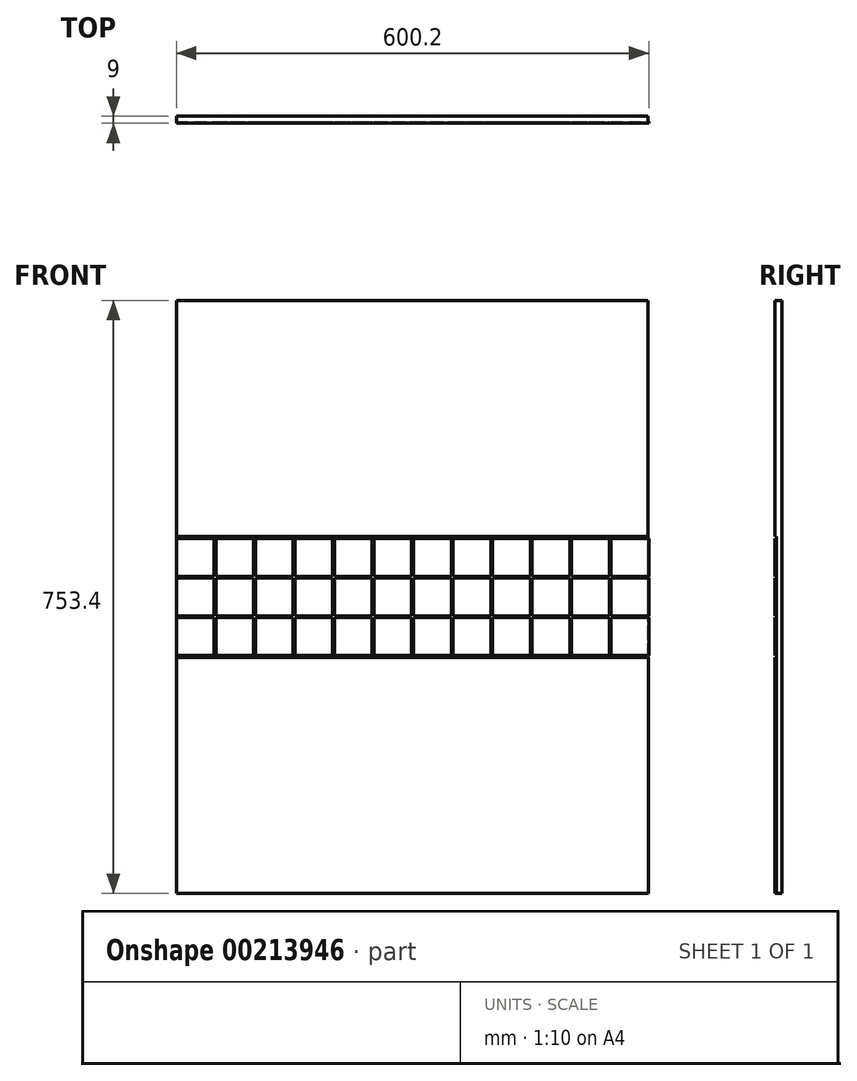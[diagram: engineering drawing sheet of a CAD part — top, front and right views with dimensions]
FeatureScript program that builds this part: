
annotation { "Feature Type Name" : "Feature", "Feature Type Description" : "" }
export const myFeature = defineFeature(function(context is Context, id is Id, definition is map)
    precondition{}
    {
        {
            var Q0;
            Q0=qCreatedBy(makeId("Front.planeOp"),FACE);
            var sketch = newSketch(context, id + "F0", { "sketchPlane" : qUnion([Q0])});
            skLineSegment(sketch, "E0.bottom", {"start": v(0, 0) * mm, "end": v(600, 0) * mm});
            skLineSegment(sketch, "E0.top", {"start": v(0, 300) * mm, "end": v(600, 300) * mm});
            skLineSegment(sketch, "E0.left", {"start": v(0, 0) * mm, "end": v(0, 300) * mm});
            skLineSegment(sketch, "E0.right", {"start": v(600, 0) * mm, "end": v(600, 300) * mm});
            skLineSegment(sketch, "E1.bottom", {"start": v(0, 350.5) * mm, "end": v(48, 350.5) * mm});
            skLineSegment(sketch, "E1.top", {"start": v(0, 302.5) * mm, "end": v(48, 302.5) * mm});
            skLineSegment(sketch, "E1.left", {"start": v(0, 302.5) * mm, "end": v(0, 350.5) * mm});
            skLineSegment(sketch, "E1.right", {"start": v(48, 302.5) * mm, "end": v(48, 350.5) * mm});
            skLineSegment(sketch, "E2.bottom", {"start": v(0, 453.4) * mm, "end": v(599.37, 453.4) * mm});
            skLineSegment(sketch, "E2.top", {"start": v(0, 753.4) * mm, "end": v(599.37, 753.4) * mm});
            skLineSegment(sketch, "E2.left", {"start": v(0, 453.4) * mm, "end": v(0, 753.4) * mm});
            skLineSegment(sketch, "E2.right", {"start": v(599.37, 453.4) * mm, "end": v(599.37, 753.4) * mm});
            skLineSegment(sketch, "E3.0.1.0", {"start": v(48, 352.7) * mm, "end": v(48, 400.7) * mm});
            skLineSegment(sketch, "E3.0.1.1", {"start": v(0, 352.7) * mm, "end": v(0, 400.7) * mm});
            skLineSegment(sketch, "E3.0.1.2", {"start": v(0, 352.7) * mm, "end": v(48, 352.7) * mm});
            skLineSegment(sketch, "E3.0.1.3", {"start": v(0, 400.7) * mm, "end": v(48, 400.7) * mm});
            skLineSegment(sketch, "E3.0.2.0", {"start": v(48, 402.9) * mm, "end": v(48, 450.9) * mm});
            skLineSegment(sketch, "E3.0.2.1", {"start": v(0, 402.9) * mm, "end": v(0, 450.9) * mm});
            skLineSegment(sketch, "E3.0.2.2", {"start": v(0, 402.9) * mm, "end": v(48, 402.9) * mm});
            skLineSegment(sketch, "E3.0.2.3", {"start": v(0, 450.9) * mm, "end": v(48, 450.9) * mm});
            skLineSegment(sketch, "E3.1.0.0", {"start": v(98.2, 302.5) * mm, "end": v(98.2, 350.5) * mm});
            skLineSegment(sketch, "E3.1.0.1", {"start": v(50.2, 302.5) * mm, "end": v(50.2, 350.5) * mm});
            skLineSegment(sketch, "E3.1.0.2", {"start": v(50.2, 302.5) * mm, "end": v(98.2, 302.5) * mm});
            skLineSegment(sketch, "E3.1.0.3", {"start": v(50.2, 350.5) * mm, "end": v(98.2, 350.5) * mm});
            skLineSegment(sketch, "E3.1.1.0", {"start": v(98.2, 352.7) * mm, "end": v(98.2, 400.7) * mm});
            skLineSegment(sketch, "E3.1.1.1", {"start": v(50.2, 352.7) * mm, "end": v(50.2, 400.7) * mm});
            skLineSegment(sketch, "E3.1.1.2", {"start": v(50.2, 352.7) * mm, "end": v(98.2, 352.7) * mm});
            skLineSegment(sketch, "E3.1.1.3", {"start": v(50.2, 400.7) * mm, "end": v(98.2, 400.7) * mm});
            skLineSegment(sketch, "E3.1.2.0", {"start": v(98.2, 402.9) * mm, "end": v(98.2, 450.9) * mm});
            skLineSegment(sketch, "E3.1.2.1", {"start": v(50.2, 402.9) * mm, "end": v(50.2, 450.9) * mm});
            skLineSegment(sketch, "E3.1.2.2", {"start": v(50.2, 402.9) * mm, "end": v(98.2, 402.9) * mm});
            skLineSegment(sketch, "E3.1.2.3", {"start": v(50.2, 450.9) * mm, "end": v(98.2, 450.9) * mm});
            skLineSegment(sketch, "E3.2.0.0", {"start": v(148.4, 302.5) * mm, "end": v(148.4, 350.5) * mm});
            skLineSegment(sketch, "E3.2.0.1", {"start": v(100.4, 302.5) * mm, "end": v(100.4, 350.5) * mm});
            skLineSegment(sketch, "E3.2.0.2", {"start": v(100.4, 302.5) * mm, "end": v(148.4, 302.5) * mm});
            skLineSegment(sketch, "E3.2.0.3", {"start": v(100.4, 350.5) * mm, "end": v(148.4, 350.5) * mm});
            skLineSegment(sketch, "E3.2.1.0", {"start": v(148.4, 352.7) * mm, "end": v(148.4, 400.7) * mm});
            skLineSegment(sketch, "E3.2.1.1", {"start": v(100.4, 352.7) * mm, "end": v(100.4, 400.7) * mm});
            skLineSegment(sketch, "E3.2.1.2", {"start": v(100.4, 352.7) * mm, "end": v(148.4, 352.7) * mm});
            skLineSegment(sketch, "E3.2.1.3", {"start": v(100.4, 400.7) * mm, "end": v(148.4, 400.7) * mm});
            skLineSegment(sketch, "E3.2.2.0", {"start": v(148.4, 402.9) * mm, "end": v(148.4, 450.9) * mm});
            skLineSegment(sketch, "E3.2.2.1", {"start": v(100.4, 402.9) * mm, "end": v(100.4, 450.9) * mm});
            skLineSegment(sketch, "E3.2.2.2", {"start": v(100.4, 402.9) * mm, "end": v(148.4, 402.9) * mm});
            skLineSegment(sketch, "E3.2.2.3", {"start": v(100.4, 450.9) * mm, "end": v(148.4, 450.9) * mm});
            skLineSegment(sketch, "E3.3.0.0", {"start": v(198.6, 302.5) * mm, "end": v(198.6, 350.5) * mm});
            skLineSegment(sketch, "E3.3.0.1", {"start": v(150.6, 302.5) * mm, "end": v(150.6, 350.5) * mm});
            skLineSegment(sketch, "E3.3.0.2", {"start": v(150.6, 302.5) * mm, "end": v(198.6, 302.5) * mm});
            skLineSegment(sketch, "E3.3.0.3", {"start": v(150.6, 350.5) * mm, "end": v(198.6, 350.5) * mm});
            skLineSegment(sketch, "E3.3.1.0", {"start": v(198.6, 352.7) * mm, "end": v(198.6, 400.7) * mm});
            skLineSegment(sketch, "E3.3.1.1", {"start": v(150.6, 352.7) * mm, "end": v(150.6, 400.7) * mm});
            skLineSegment(sketch, "E3.3.1.2", {"start": v(150.6, 352.7) * mm, "end": v(198.6, 352.7) * mm});
            skLineSegment(sketch, "E3.3.1.3", {"start": v(150.6, 400.7) * mm, "end": v(198.6, 400.7) * mm});
            skLineSegment(sketch, "E3.3.2.0", {"start": v(198.6, 402.9) * mm, "end": v(198.6, 450.9) * mm});
            skLineSegment(sketch, "E3.3.2.1", {"start": v(150.6, 402.9) * mm, "end": v(150.6, 450.9) * mm});
            skLineSegment(sketch, "E3.3.2.2", {"start": v(150.6, 402.9) * mm, "end": v(198.6, 402.9) * mm});
            skLineSegment(sketch, "E3.3.2.3", {"start": v(150.6, 450.9) * mm, "end": v(198.6, 450.9) * mm});
            skLineSegment(sketch, "E3.4.0.0", {"start": v(248.8, 302.5) * mm, "end": v(248.8, 350.5) * mm});
            skLineSegment(sketch, "E3.4.0.1", {"start": v(200.8, 302.5) * mm, "end": v(200.8, 350.5) * mm});
            skLineSegment(sketch, "E3.4.0.2", {"start": v(200.8, 302.5) * mm, "end": v(248.8, 302.5) * mm});
            skLineSegment(sketch, "E3.4.0.3", {"start": v(200.8, 350.5) * mm, "end": v(248.8, 350.5) * mm});
            skLineSegment(sketch, "E3.4.1.0", {"start": v(248.8, 352.7) * mm, "end": v(248.8, 400.7) * mm});
            skLineSegment(sketch, "E3.4.1.1", {"start": v(200.8, 352.7) * mm, "end": v(200.8, 400.7) * mm});
            skLineSegment(sketch, "E3.4.1.2", {"start": v(200.8, 352.7) * mm, "end": v(248.8, 352.7) * mm});
            skLineSegment(sketch, "E3.4.1.3", {"start": v(200.8, 400.7) * mm, "end": v(248.8, 400.7) * mm});
            skLineSegment(sketch, "E3.4.2.0", {"start": v(248.8, 402.9) * mm, "end": v(248.8, 450.9) * mm});
            skLineSegment(sketch, "E3.4.2.1", {"start": v(200.8, 402.9) * mm, "end": v(200.8, 450.9) * mm});
            skLineSegment(sketch, "E3.4.2.2", {"start": v(200.8, 402.9) * mm, "end": v(248.8, 402.9) * mm});
            skLineSegment(sketch, "E3.4.2.3", {"start": v(200.8, 450.9) * mm, "end": v(248.8, 450.9) * mm});
            skLineSegment(sketch, "E3.5.0.0", {"start": v(299, 302.5) * mm, "end": v(299, 350.5) * mm});
            skLineSegment(sketch, "E3.5.0.1", {"start": v(251, 302.5) * mm, "end": v(251, 350.5) * mm});
            skLineSegment(sketch, "E3.5.0.2", {"start": v(251, 302.5) * mm, "end": v(299, 302.5) * mm});
            skLineSegment(sketch, "E3.5.0.3", {"start": v(251, 350.5) * mm, "end": v(299, 350.5) * mm});
            skLineSegment(sketch, "E3.5.1.0", {"start": v(299, 352.7) * mm, "end": v(299, 400.7) * mm});
            skLineSegment(sketch, "E3.5.1.1", {"start": v(251, 352.7) * mm, "end": v(251, 400.7) * mm});
            skLineSegment(sketch, "E3.5.1.2", {"start": v(251, 352.7) * mm, "end": v(299, 352.7) * mm});
            skLineSegment(sketch, "E3.5.1.3", {"start": v(251, 400.7) * mm, "end": v(299, 400.7) * mm});
            skLineSegment(sketch, "E3.5.2.0", {"start": v(299, 402.9) * mm, "end": v(299, 450.9) * mm});
            skLineSegment(sketch, "E3.5.2.1", {"start": v(251, 402.9) * mm, "end": v(251, 450.9) * mm});
            skLineSegment(sketch, "E3.5.2.2", {"start": v(251, 402.9) * mm, "end": v(299, 402.9) * mm});
            skLineSegment(sketch, "E3.5.2.3", {"start": v(251, 450.9) * mm, "end": v(299, 450.9) * mm});
            skLineSegment(sketch, "E3.6.0.0", {"start": v(349.2, 302.5) * mm, "end": v(349.2, 350.5) * mm});
            skLineSegment(sketch, "E3.6.0.1", {"start": v(301.2, 302.5) * mm, "end": v(301.2, 350.5) * mm});
            skLineSegment(sketch, "E3.6.0.2", {"start": v(301.2, 302.5) * mm, "end": v(349.2, 302.5) * mm});
            skLineSegment(sketch, "E3.6.0.3", {"start": v(301.2, 350.5) * mm, "end": v(349.2, 350.5) * mm});
            skLineSegment(sketch, "E3.6.1.0", {"start": v(349.2, 352.7) * mm, "end": v(349.2, 400.7) * mm});
            skLineSegment(sketch, "E3.6.1.1", {"start": v(301.2, 352.7) * mm, "end": v(301.2, 400.7) * mm});
            skLineSegment(sketch, "E3.6.1.2", {"start": v(301.2, 352.7) * mm, "end": v(349.2, 352.7) * mm});
            skLineSegment(sketch, "E3.6.1.3", {"start": v(301.2, 400.7) * mm, "end": v(349.2, 400.7) * mm});
            skLineSegment(sketch, "E3.6.2.0", {"start": v(349.2, 402.9) * mm, "end": v(349.2, 450.9) * mm});
            skLineSegment(sketch, "E3.6.2.1", {"start": v(301.2, 402.9) * mm, "end": v(301.2, 450.9) * mm});
            skLineSegment(sketch, "E3.6.2.2", {"start": v(301.2, 402.9) * mm, "end": v(349.2, 402.9) * mm});
            skLineSegment(sketch, "E3.6.2.3", {"start": v(301.2, 450.9) * mm, "end": v(349.2, 450.9) * mm});
            skLineSegment(sketch, "E3.7.0.0", {"start": v(399.4, 302.5) * mm, "end": v(399.4, 350.5) * mm});
            skLineSegment(sketch, "E3.7.0.1", {"start": v(351.4, 302.5) * mm, "end": v(351.4, 350.5) * mm});
            skLineSegment(sketch, "E3.7.0.2", {"start": v(351.4, 302.5) * mm, "end": v(399.4, 302.5) * mm});
            skLineSegment(sketch, "E3.7.0.3", {"start": v(351.4, 350.5) * mm, "end": v(399.4, 350.5) * mm});
            skLineSegment(sketch, "E3.7.1.0", {"start": v(399.4, 352.7) * mm, "end": v(399.4, 400.7) * mm});
            skLineSegment(sketch, "E3.7.1.1", {"start": v(351.4, 352.7) * mm, "end": v(351.4, 400.7) * mm});
            skLineSegment(sketch, "E3.7.1.2", {"start": v(351.4, 352.7) * mm, "end": v(399.4, 352.7) * mm});
            skLineSegment(sketch, "E3.7.1.3", {"start": v(351.4, 400.7) * mm, "end": v(399.4, 400.7) * mm});
            skLineSegment(sketch, "E3.7.2.0", {"start": v(399.4, 402.9) * mm, "end": v(399.4, 450.9) * mm});
            skLineSegment(sketch, "E3.7.2.1", {"start": v(351.4, 402.9) * mm, "end": v(351.4, 450.9) * mm});
            skLineSegment(sketch, "E3.7.2.2", {"start": v(351.4, 402.9) * mm, "end": v(399.4, 402.9) * mm});
            skLineSegment(sketch, "E3.7.2.3", {"start": v(351.4, 450.9) * mm, "end": v(399.4, 450.9) * mm});
            skLineSegment(sketch, "E3.8.0.0", {"start": v(449.6, 302.5) * mm, "end": v(449.6, 350.5) * mm});
            skLineSegment(sketch, "E3.8.0.1", {"start": v(401.6, 302.5) * mm, "end": v(401.6, 350.5) * mm});
            skLineSegment(sketch, "E3.8.0.2", {"start": v(401.6, 302.5) * mm, "end": v(449.6, 302.5) * mm});
            skLineSegment(sketch, "E3.8.0.3", {"start": v(401.6, 350.5) * mm, "end": v(449.6, 350.5) * mm});
            skLineSegment(sketch, "E3.8.1.0", {"start": v(449.6, 352.7) * mm, "end": v(449.6, 400.7) * mm});
            skLineSegment(sketch, "E3.8.1.1", {"start": v(401.6, 352.7) * mm, "end": v(401.6, 400.7) * mm});
            skLineSegment(sketch, "E3.8.1.2", {"start": v(401.6, 352.7) * mm, "end": v(449.6, 352.7) * mm});
            skLineSegment(sketch, "E3.8.1.3", {"start": v(401.6, 400.7) * mm, "end": v(449.6, 400.7) * mm});
            skLineSegment(sketch, "E3.8.2.0", {"start": v(449.6, 402.9) * mm, "end": v(449.6, 450.9) * mm});
            skLineSegment(sketch, "E3.8.2.1", {"start": v(401.6, 402.9) * mm, "end": v(401.6, 450.9) * mm});
            skLineSegment(sketch, "E3.8.2.2", {"start": v(401.6, 402.9) * mm, "end": v(449.6, 402.9) * mm});
            skLineSegment(sketch, "E3.8.2.3", {"start": v(401.6, 450.9) * mm, "end": v(449.6, 450.9) * mm});
            skLineSegment(sketch, "E3.9.0.0", {"start": v(499.8, 302.5) * mm, "end": v(499.8, 350.5) * mm});
            skLineSegment(sketch, "E3.9.0.1", {"start": v(451.8, 302.5) * mm, "end": v(451.8, 350.5) * mm});
            skLineSegment(sketch, "E3.9.0.2", {"start": v(451.8, 302.5) * mm, "end": v(499.8, 302.5) * mm});
            skLineSegment(sketch, "E3.9.0.3", {"start": v(451.8, 350.5) * mm, "end": v(499.8, 350.5) * mm});
            skLineSegment(sketch, "E3.9.1.0", {"start": v(499.8, 352.7) * mm, "end": v(499.8, 400.7) * mm});
            skLineSegment(sketch, "E3.9.1.1", {"start": v(451.8, 352.7) * mm, "end": v(451.8, 400.7) * mm});
            skLineSegment(sketch, "E3.9.1.2", {"start": v(451.8, 352.7) * mm, "end": v(499.8, 352.7) * mm});
            skLineSegment(sketch, "E3.9.1.3", {"start": v(451.8, 400.7) * mm, "end": v(499.8, 400.7) * mm});
            skLineSegment(sketch, "E3.9.2.0", {"start": v(499.8, 402.9) * mm, "end": v(499.8, 450.9) * mm});
            skLineSegment(sketch, "E3.9.2.1", {"start": v(451.8, 402.9) * mm, "end": v(451.8, 450.9) * mm});
            skLineSegment(sketch, "E3.9.2.2", {"start": v(451.8, 402.9) * mm, "end": v(499.8, 402.9) * mm});
            skLineSegment(sketch, "E3.9.2.3", {"start": v(451.8, 450.9) * mm, "end": v(499.8, 450.9) * mm});
            skLineSegment(sketch, "E3.10.0.0", {"start": v(550, 302.5) * mm, "end": v(550, 350.5) * mm});
            skLineSegment(sketch, "E3.10.0.1", {"start": v(502, 302.5) * mm, "end": v(502, 350.5) * mm});
            skLineSegment(sketch, "E3.10.0.2", {"start": v(502, 302.5) * mm, "end": v(550, 302.5) * mm});
            skLineSegment(sketch, "E3.10.0.3", {"start": v(502, 350.5) * mm, "end": v(550, 350.5) * mm});
            skLineSegment(sketch, "E3.10.1.0", {"start": v(550, 352.7) * mm, "end": v(550, 400.7) * mm});
            skLineSegment(sketch, "E3.10.1.1", {"start": v(502, 352.7) * mm, "end": v(502, 400.7) * mm});
            skLineSegment(sketch, "E3.10.1.2", {"start": v(502, 352.7) * mm, "end": v(550, 352.7) * mm});
            skLineSegment(sketch, "E3.10.1.3", {"start": v(502, 400.7) * mm, "end": v(550, 400.7) * mm});
            skLineSegment(sketch, "E3.10.2.0", {"start": v(550, 402.9) * mm, "end": v(550, 450.9) * mm});
            skLineSegment(sketch, "E3.10.2.1", {"start": v(502, 402.9) * mm, "end": v(502, 450.9) * mm});
            skLineSegment(sketch, "E3.10.2.2", {"start": v(502, 402.9) * mm, "end": v(550, 402.9) * mm});
            skLineSegment(sketch, "E3.10.2.3", {"start": v(502, 450.9) * mm, "end": v(550, 450.9) * mm});
            skLineSegment(sketch, "E3.11.0.0", {"start": v(600.2, 302.5) * mm, "end": v(600.2, 350.5) * mm});
            skLineSegment(sketch, "E3.11.0.1", {"start": v(552.2, 302.5) * mm, "end": v(552.2, 350.5) * mm});
            skLineSegment(sketch, "E3.11.0.2", {"start": v(552.2, 302.5) * mm, "end": v(600.2, 302.5) * mm});
            skLineSegment(sketch, "E3.11.0.3", {"start": v(552.2, 350.5) * mm, "end": v(600.2, 350.5) * mm});
            skLineSegment(sketch, "E3.11.1.0", {"start": v(600.2, 352.7) * mm, "end": v(600.2, 400.7) * mm});
            skLineSegment(sketch, "E3.11.1.1", {"start": v(552.2, 352.7) * mm, "end": v(552.2, 400.7) * mm});
            skLineSegment(sketch, "E3.11.1.2", {"start": v(552.2, 352.7) * mm, "end": v(600.2, 352.7) * mm});
            skLineSegment(sketch, "E3.11.1.3", {"start": v(552.2, 400.7) * mm, "end": v(600.2, 400.7) * mm});
            skLineSegment(sketch, "E3.11.2.0", {"start": v(600.2, 402.9) * mm, "end": v(600.2, 450.9) * mm});
            skLineSegment(sketch, "E3.11.2.1", {"start": v(552.2, 402.9) * mm, "end": v(552.2, 450.9) * mm});
            skLineSegment(sketch, "E3.11.2.2", {"start": v(552.2, 402.9) * mm, "end": v(600.2, 402.9) * mm});
            skLineSegment(sketch, "E3.11.2.3", {"start": v(552.2, 450.9) * mm, "end": v(600.2, 450.9) * mm});
            skLineSegment(sketch, "E3.direction1", {"start": v(0, 302.5) * mm, "end": v(50.2, 302.5) * mm, "construction": true});
            skLineSegment(sketch, "E3.direction2", {"start": v(0, 302.5) * mm, "end": v(0, 352.7) * mm, "construction": true});
            skSolve(sketch);
        }
        {
            var Q0;
            Q0 = qSketchRegion(id + "F0", true);
            extrude(context, id + "F1", {"entities" : qUnion([Q0]), "depth" : 2 * mm});
        }
        {
            var Q0;
            Q0=makeQuery(id+"F1.opExtrude","CAP_FACE",FACE,{"disambiguationData":[OSD([sQuery(id+"F0.wireOp",EDGE,"E2.bottom"),sQuery(id+"F0.wireOp",EDGE,"E2.top"),sQuery(id+"F0.wireOp",EDGE,"E2.left"),sQuery(id+"F0.wireOp",EDGE,"E2.right")])],"isStart":true});
            var sketch = newSketch(context, id + "F2", { "sketchPlane" : qUnion([Q0])});
            skLineSegment(sketch, "E4.bottom", {"start": v(-599.37, 753.4) * mm, "end": v(0, 753.4) * mm});
            skLineSegment(sketch, "E4.top", {"start": v(-599.37, 0) * mm, "end": v(0, 0) * mm});
            skLineSegment(sketch, "E4.left", {"start": v(-599.37, 753.4) * mm, "end": v(-599.37, 0) * mm});
            skLineSegment(sketch, "E4.right", {"start": v(0, 753.4) * mm, "end": v(0, 0) * mm});
            skSolve(sketch);
        }
        {
            var Q0;
            Q0 = qSketchRegion(id + "F2", true);
            extrude(context, id + "F3", {"entities" : qUnion([Q0]), "operationType" : NewBodyOperationType.ADD, "depth" : 7 * mm});
        }
    });
